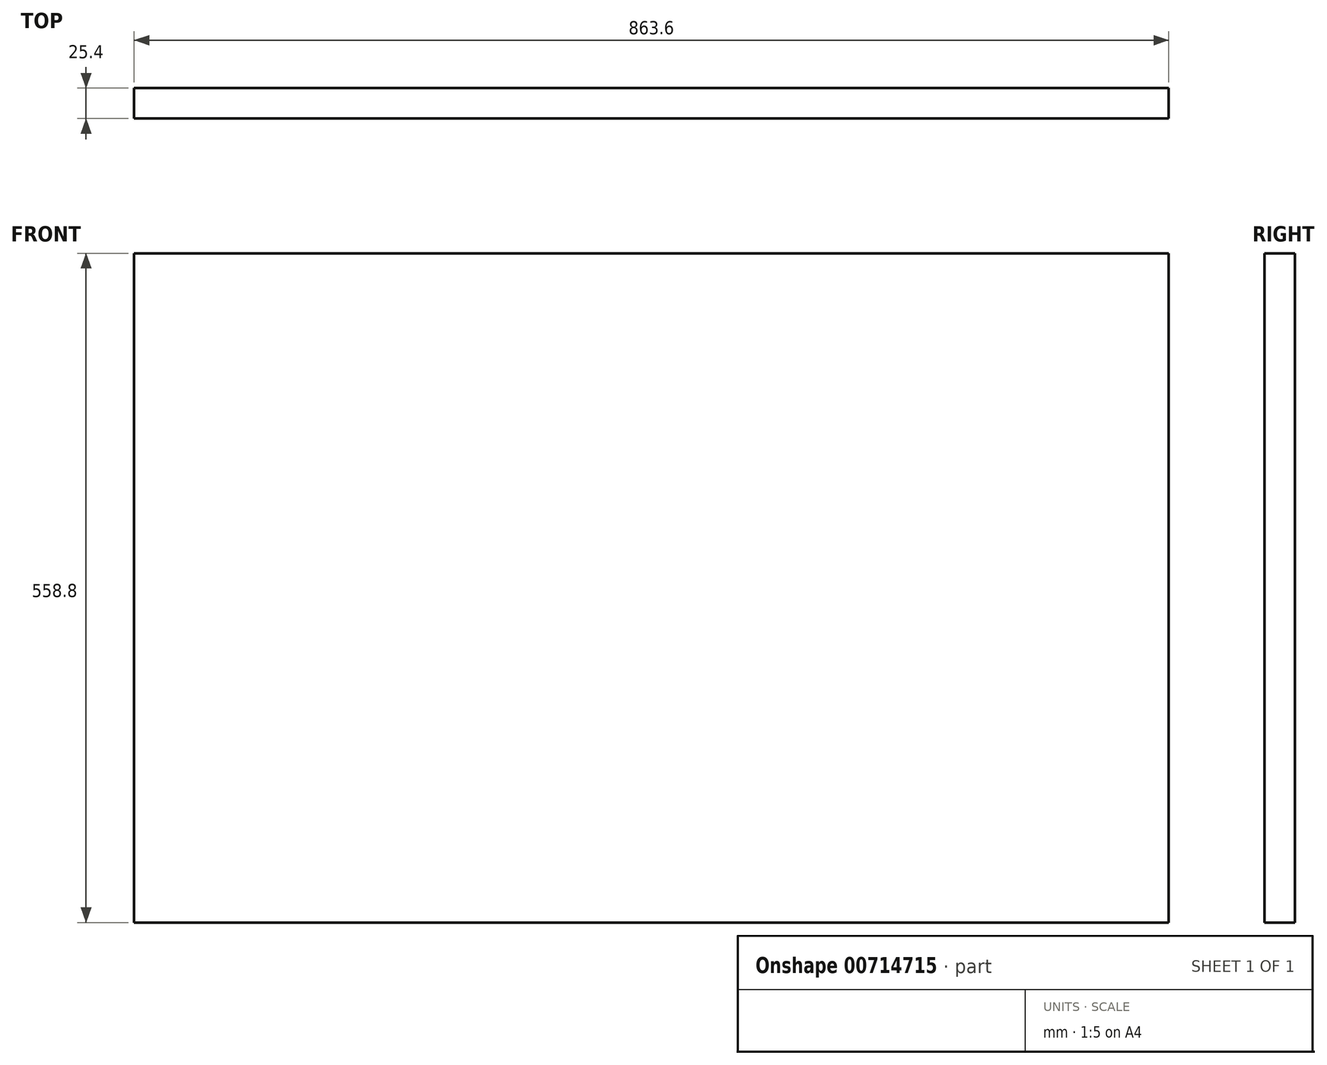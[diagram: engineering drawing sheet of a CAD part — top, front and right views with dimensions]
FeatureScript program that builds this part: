
annotation { "Feature Type Name" : "Feature", "Feature Type Description" : "" }
export const myFeature = defineFeature(function(context is Context, id is Id, definition is map)
    precondition{}
    {
        {
            var Q0;
            Q0=qCreatedBy(makeId("Front.planeOp"),FACE);
            var sketch = newSketch(context, id + "F0", { "sketchPlane" : qUnion([Q0])});
            skLineSegment(sketch, "E0.bottom", {"start": v(431.8, -279.4) * mm, "end": v(-431.8, -279.4) * mm});
            skLineSegment(sketch, "E0.top", {"start": v(431.8, 279.4) * mm, "end": v(-431.8, 279.4) * mm});
            skLineSegment(sketch, "E0.left", {"start": v(431.8, -279.4) * mm, "end": v(431.8, 279.4) * mm});
            skLineSegment(sketch, "E0.right", {"start": v(-431.8, -279.4) * mm, "end": v(-431.8, 279.4) * mm});
            skPoint(sketch, "E0.middle", {"position": v(0, 0) * mm});
            skSolve(sketch);
        }
        {
            var Q0;
            Q0 = qSketchRegion(id + "F0", true);
            extrude(context, id + "F1", {"entities" : qUnion([Q0]), "depth" : 25.4 * mm, "offsetDistance" : 25.4 * mm});
        }
    });
